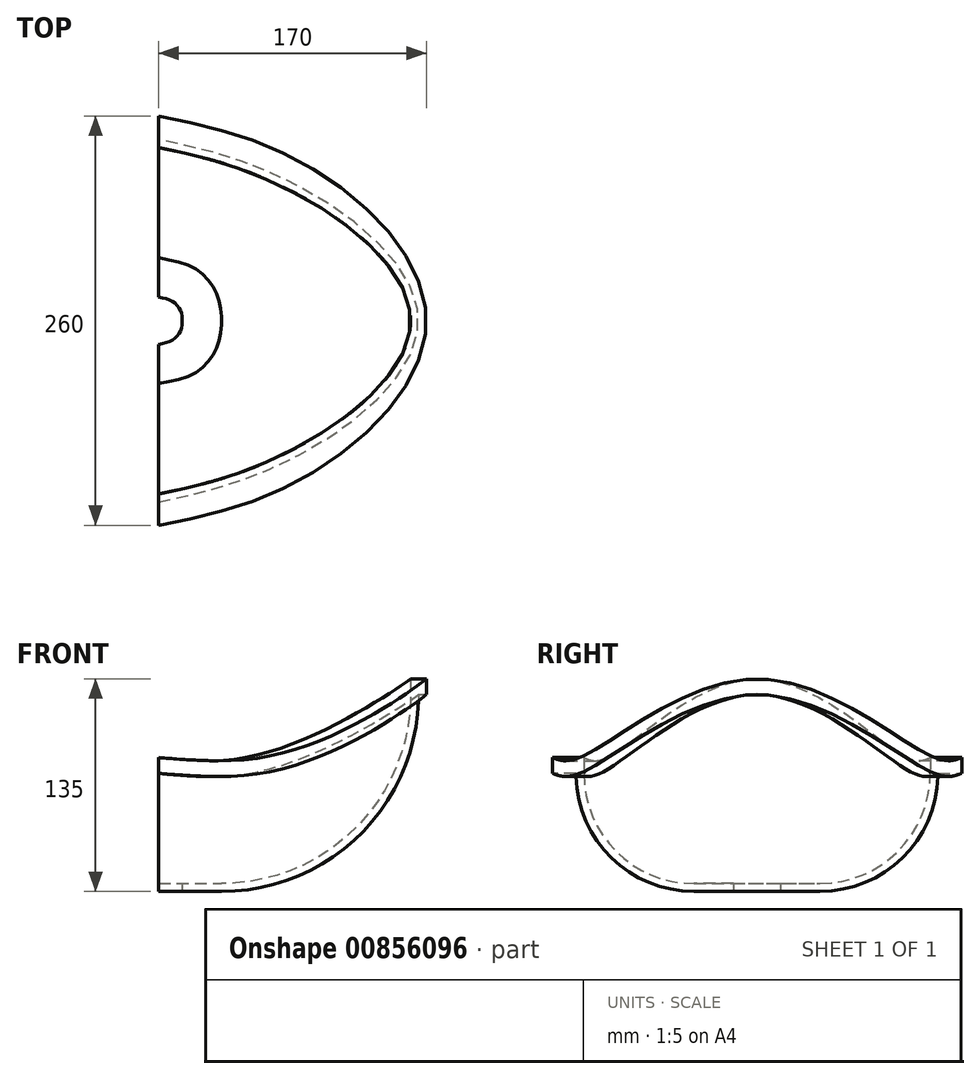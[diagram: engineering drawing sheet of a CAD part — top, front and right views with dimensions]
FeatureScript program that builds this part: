
annotation { "Feature Type Name" : "Feature", "Feature Type Description" : "" }
export const myFeature = defineFeature(function(context is Context, id is Id, definition is map)
    precondition{}
    {
        {
            var Q0;
            Q0=qCreatedBy(makeId("Front.planeOp"),FACE);
            var sketch = newSketch(context, id + "F0", { "sketchPlane" : qUnion([Q0])});
            skLineSegment(sketch, "E0.bottom", {"start": v(15, 5) * mm, "end": v(40, 5) * mm});
            skLineSegment(sketch, "E0.top", {"start": v(15, 0) * mm, "end": v(40, 0) * mm});
            skLineSegment(sketch, "E0.left", {"start": v(15, 5) * mm, "end": v(15, 0) * mm});
            skLineSegment(sketch, "E0.right", {"start": v(40, 5) * mm, "end": v(40, 0) * mm, "construction": true});
            skLineSegment(sketch, "E1.bottom", {"start": v(160, 135) * mm, "end": v(170, 135) * mm});
            skLineSegment(sketch, "E1.top", {"start": v(165, 125) * mm, "end": v(170, 125) * mm});
            skLineSegment(sketch, "E1.left", {"start": v(160, 135) * mm, "end": v(160, 125) * mm});
            skLineSegment(sketch, "E1.right", {"start": v(170, 135) * mm, "end": v(170, 125) * mm});
            skArc(sketch, "E2", {"start": v(40, 0) * mm, "mid": v(128.39, 36.61) * mm, "end": v(165, 125) * mm});
            skArc(sketch, "E3", {"start": v(40, 5) * mm, "mid": v(124.85, 40.15) * mm, "end": v(160, 125) * mm});
            skLineSegment(sketch, "E4", {"start": v(0, 0) * mm, "end": v(0, 50) * mm, "construction": true});
            skSolve(sketch);
        }
        {
            var Q0;
            Q0=sQuery(id+"F0.wireOp",EDGE,"E4");
            cPlane(context, id + "F1", {"entities" : qUnion([Q0]), "cplaneType" : CPlaneType.LINE_ANGLE, "offset" : 25 * mm, "angle" : 30 * degree, "oppositeDirection" : true, "width" : 150 * mm, "height" : 150 * mm});
        }
        {
            var Q0;
            Q0=qCreatedBy(id+"F1.planeOp",FACE);
            var sketch = newSketch(context, id + "F2", { "sketchPlane" : qUnion([Q0])});
            skLineSegment(sketch, "E5.bottom", {"start": v(15, 5) * mm, "end": v(40, 5) * mm});
            skLineSegment(sketch, "E5.top", {"start": v(15, 0) * mm, "end": v(40, 0) * mm});
            skLineSegment(sketch, "E5.left", {"start": v(15, 5) * mm, "end": v(15, 0) * mm});
            skLineSegment(sketch, "E5.right", {"start": v(40, 5) * mm, "end": v(40, 0) * mm, "construction": true});
            skLineSegment(sketch, "E6.bottom", {"start": v(110, 85) * mm, "end": v(130, 85) * mm});
            skLineSegment(sketch, "E6.top", {"start": v(115, 75) * mm, "end": v(130, 75) * mm});
            skLineSegment(sketch, "E6.left", {"start": v(110, 85) * mm, "end": v(110, 75) * mm});
            skLineSegment(sketch, "E6.right", {"start": v(130, 85) * mm, "end": v(130, 75) * mm});
            skArc(sketch, "E7", {"start": v(40, 0) * mm, "mid": v(93.03, 21.97) * mm, "end": v(115, 75) * mm});
            skArc(sketch, "E8", {"start": v(40, 5) * mm, "mid": v(89.5, 25.5) * mm, "end": v(110, 75) * mm});
            skLineSegment(sketch, "E9", {"start": v(0, 0) * mm, "end": v(0, 50) * mm, "construction": true});
            skSolve(sketch);
        }
        {
            var Q0;
            Q0=sQuery(id+"F0.wireOp",EDGE,"E4");
            cPlane(context, id + "F3", {"entities" : qUnion([Q0]), "cplaneType" : CPlaneType.LINE_ANGLE, "offset" : 25 * mm, "angle" : 150 * degree, "oppositeDirection" : true, "width" : 150 * mm, "height" : 150 * mm});
        }
        {
            var Q0;
            Q0=qCreatedBy(id+"F3.planeOp",FACE);
            var sketch = newSketch(context, id + "F4", { "sketchPlane" : qUnion([Q0])});
            skLineSegment(sketch, "E10.bottom", {"start": v(15, 5) * mm, "end": v(40, 5) * mm});
            skLineSegment(sketch, "E10.top", {"start": v(15, 0) * mm, "end": v(40, 0) * mm});
            skLineSegment(sketch, "E10.left", {"start": v(15, 5) * mm, "end": v(15, 0) * mm});
            skLineSegment(sketch, "E10.right", {"start": v(40, 5) * mm, "end": v(40, 0) * mm, "construction": true});
            skLineSegment(sketch, "E11.bottom", {"start": v(110, 85) * mm, "end": v(130, 85) * mm});
            skLineSegment(sketch, "E11.top", {"start": v(115, 75) * mm, "end": v(130, 75) * mm});
            skLineSegment(sketch, "E11.left", {"start": v(110, 85) * mm, "end": v(110, 75) * mm});
            skLineSegment(sketch, "E11.right", {"start": v(130, 85) * mm, "end": v(130, 75) * mm});
            skArc(sketch, "E12", {"start": v(40, 0) * mm, "mid": v(93.03, 21.97) * mm, "end": v(115, 75) * mm});
            skArc(sketch, "E13", {"start": v(40, 5) * mm, "mid": v(89.5, 25.5) * mm, "end": v(110, 75) * mm});
            skLineSegment(sketch, "E14", {"start": v(0, 0) * mm, "end": v(0, 50) * mm, "construction": true});
            skSolve(sketch);
        }
        {
            var Q0;
            Q0=qCreatedBy(makeId("Right.planeOp"),FACE);
            var sketch = newSketch(context, id + "F5", { "sketchPlane" : qUnion([Q0])});
            skLineSegment(sketch, "E15.bottom", {"start": v(15, 5) * mm, "end": v(40, 5) * mm});
            skLineSegment(sketch, "E15.top", {"start": v(15, 0) * mm, "end": v(40, 0) * mm});
            skLineSegment(sketch, "E15.left", {"start": v(15, 5) * mm, "end": v(15, 0) * mm});
            skLineSegment(sketch, "E15.right", {"start": v(40, 5) * mm, "end": v(40, 0) * mm, "construction": true});
            skLineSegment(sketch, "E16.bottom", {"start": v(110, 85) * mm, "end": v(130, 85) * mm});
            skLineSegment(sketch, "E16.top", {"start": v(115, 75) * mm, "end": v(130, 75) * mm});
            skLineSegment(sketch, "E16.left", {"start": v(110, 85) * mm, "end": v(110, 75) * mm});
            skLineSegment(sketch, "E16.right", {"start": v(130, 85) * mm, "end": v(130, 75) * mm});
            skArc(sketch, "E17", {"start": v(40, 0) * mm, "mid": v(93.03, 21.97) * mm, "end": v(115, 75) * mm});
            skArc(sketch, "E18", {"start": v(40, 5) * mm, "mid": v(89.5, 25.5) * mm, "end": v(110, 75) * mm});
            skLineSegment(sketch, "E19", {"start": v(0, 0) * mm, "end": v(0, 50) * mm, "construction": true});
            skSolve(sketch);
        }
        {
            var Q0;
            Q0=sQuery(id+"F5.wireOp",EDGE,"E19");
            cPlane(context, id + "F6", {"entities" : qUnion([Q0]), "cplaneType" : CPlaneType.LINE_ANGLE, "offset" : 25 * mm, "angle" : 180 * degree, "width" : 150 * mm, "height" : 150 * mm});
        }
        {
            var Q0;
            Q0=qCreatedBy(id+"F6.planeOp",FACE);
            var sketch = newSketch(context, id + "F7", { "sketchPlane" : qUnion([Q0])});
            skLineSegment(sketch, "E20.bottom", {"start": v(15, 5) * mm, "end": v(40, 5) * mm});
            skLineSegment(sketch, "E20.top", {"start": v(15, 0) * mm, "end": v(40, 0) * mm});
            skLineSegment(sketch, "E20.left", {"start": v(15, 5) * mm, "end": v(15, 0) * mm});
            skLineSegment(sketch, "E20.right", {"start": v(40, 5) * mm, "end": v(40, 0) * mm, "construction": true});
            skLineSegment(sketch, "E21.bottom", {"start": v(110, 85) * mm, "end": v(130, 85) * mm});
            skLineSegment(sketch, "E21.top", {"start": v(115, 75) * mm, "end": v(130, 75) * mm});
            skLineSegment(sketch, "E21.left", {"start": v(110, 85) * mm, "end": v(110, 75) * mm});
            skLineSegment(sketch, "E21.right", {"start": v(130, 85) * mm, "end": v(130, 75) * mm});
            skArc(sketch, "E22", {"start": v(40, 0) * mm, "mid": v(93.03, 21.97) * mm, "end": v(115, 75) * mm});
            skArc(sketch, "E23", {"start": v(40, 5) * mm, "mid": v(89.5, 25.5) * mm, "end": v(110, 75) * mm});
            skLineSegment(sketch, "E24", {"start": v(0, 0) * mm, "end": v(0, 50) * mm, "construction": true});
            skSolve(sketch);
        }
        {
            var Q0;
            Q0=makeQuery(id+"F7.imprint","IMPRINT",FACE,{"disambiguationData":[TD([[makeQuery(id+"F7.imprint","IMPRINT",EDGE,{"derivedFrom":sQuery(id+"F7.wireOp",EDGE,"E20.bottom")}),-1.0]])]});
            var Q1;
            Q1=makeQuery(id+"F4.imprint","IMPRINT",FACE,{"disambiguationData":[TD([[makeQuery(id+"F4.imprint","IMPRINT",EDGE,{"derivedFrom":sQuery(id+"F4.wireOp",EDGE,"E10.bottom")}),-1.0]])]});
            var Q2;
            Q2=makeQuery(id+"F0.imprint","IMPRINT",FACE,{"disambiguationData":[TD([[makeQuery(id+"F0.imprint","IMPRINT",EDGE,{"derivedFrom":sQuery(id+"F0.wireOp",EDGE,"E0.bottom")}),-1.0]])]});
            var Q3;
            Q3=makeQuery(id+"F2.imprint","IMPRINT",FACE,{"disambiguationData":[TD([[makeQuery(id+"F2.imprint","IMPRINT",EDGE,{"derivedFrom":sQuery(id+"F2.wireOp",EDGE,"E5.bottom")}),-1.0]])]});
            var Q4;
            Q4=makeQuery(id+"F5.imprint","IMPRINT",FACE,{"disambiguationData":[TD([[makeQuery(id+"F5.imprint","IMPRINT",EDGE,{"derivedFrom":sQuery(id+"F5.wireOp",EDGE,"E15.bottom")}),-1.0]])]});
            loft(context, id + "F8", {"sheetProfilesArray" : [{ "sheetProfileEntities" : qUnion([Q0]) }, { "sheetProfileEntities" : qUnion([Q1]) }, { "sheetProfileEntities" : qUnion([Q2]) }, { "sheetProfileEntities" : qUnion([Q3]) }, { "sheetProfileEntities" : qUnion([Q4]) }]});
        }
    });
